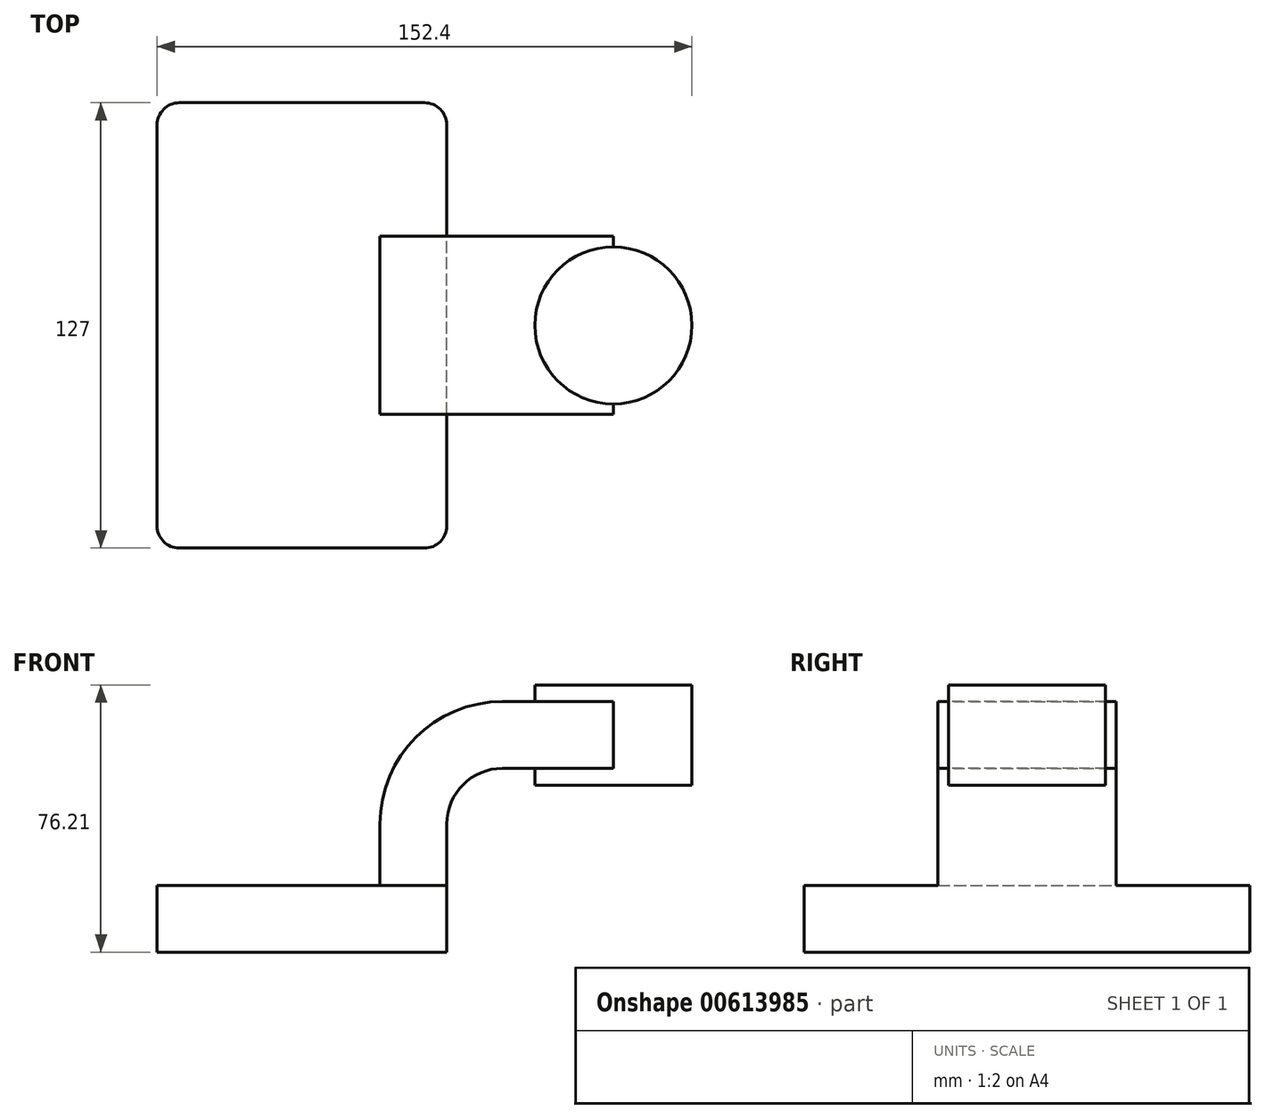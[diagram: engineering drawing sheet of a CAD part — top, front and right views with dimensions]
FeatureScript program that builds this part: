
annotation { "Feature Type Name" : "Feature", "Feature Type Description" : "" }
export const myFeature = defineFeature(function(context is Context, id is Id, definition is map)
    precondition{}
    {
        {
            var Q0;
            Q0=qCreatedBy(makeId("Front.planeOp"),FACE);
            var sketch = newSketch(context, id + "F0", { "sketchPlane" : qUnion([Q0])});
            skLineSegment(sketch, "E0.bottom", {"start": v(-41.28, -9.52) * mm, "end": v(41.28, -9.52) * mm});
            skLineSegment(sketch, "E0.top", {"start": v(-41.28, 9.53) * mm, "end": v(41.28, 9.53) * mm});
            skLineSegment(sketch, "E0.left", {"start": v(-41.27, -9.52) * mm, "end": v(-41.28, 9.53) * mm});
            skLineSegment(sketch, "E0.right", {"start": v(41.28, -9.52) * mm, "end": v(41.28, 9.53) * mm});
            skPoint(sketch, "E0.middle", {"position": v(0, 0) * mm});
            skLineSegment(sketch, "E1.bottom", {"start": v(60.32, 38.1) * mm, "end": v(111.12, 38.1) * mm});
            skLineSegment(sketch, "E1.top", {"start": v(60.32, 66.67) * mm, "end": v(111.12, 66.67) * mm});
            skLineSegment(sketch, "E1.left", {"start": v(60.32, 38.1) * mm, "end": v(60.32, 66.67) * mm});
            skLineSegment(sketch, "E1.right", {"start": v(111.12, 38.1) * mm, "end": v(111.12, 66.67) * mm});
            skPoint(sketch, "E1.middle", {"position": v(85.72, 52.39) * mm});
            skLineSegment(sketch, "E2", {"start": v(41.27, 9.53) * mm, "end": v(41.27, 27) * mm});
            skArc(sketch, "E3", {"start": v(41.27, 27) * mm, "mid": v(45.92, 38.23) * mm, "end": v(57.15, 42.88) * mm});
            skLineSegment(sketch, "E4", {"start": v(57.15, 42.88) * mm, "end": v(88.74, 42.88) * mm});
            skArc(sketch, "E5.0", {"start": v(22.22, 27) * mm, "mid": v(32.45, 51.7) * mm, "end": v(57.15, 61.93) * mm});
            skLineSegment(sketch, "E5.1", {"start": v(22.22, 9.53) * mm, "end": v(22.22, 27) * mm});
            skLineSegment(sketch, "E6.0", {"start": v(57.15, 61.93) * mm, "end": v(88.74, 61.93) * mm});
            skLineSegment(sketch, "E7", {"start": v(88.74, 42.88) * mm, "end": v(88.74, 61.93) * mm});
            skFitSpline(sketch, "E8", {"points": [v(-41.28, 9.53) * mm, v(57.15, 61.93) * mm], "startDerivative": vector(2.35, 60.88) * mm, "endDerivative": vector(125.28, -0.45) * mm});
            skLineSegment(sketch, "E9", {"start": v(88.74, 61.93) * mm, "end": v(88.74, 66.67) * mm});
            skLineSegment(sketch, "E10", {"start": v(88.74, 42.88) * mm, "end": v(88.74, 38.1) * mm});
            skSolve(sketch);
        }
        {
            var Q0;
            Q0=makeQuery(id+"F0.imprint","IMPRINT",FACE,{"disambiguationData":[TD([[makeQuery(id+"F0.imprint","IMPRINT",EDGE,{"derivedFrom":sQuery(id+"F0.wireOp",EDGE,"E0.bottom")}),1.0]])]});
            extrude(context, id + "F1", {"entities" : qUnion([Q0]), "endBound" : BoundingType.SYMMETRIC, "depth" : 127 * mm, "offsetDistance" : 25.4 * mm});
        }
        {
            var Q0;
            {var subQ0=sQuery(id+"F0.wireOp",EDGE,"E2");Q0=makeQuery(id+"F0.imprint","IMPRINT",FACE,{"disambiguationData":[TD([[makeQuery(id+"F0.imprint","IMPRINT",EDGE,{"derivedFrom":subQ0}),1.0]])]});}
            extrude(context, id + "F2", {"entities" : qUnion([Q0]), "operationType" : NewBodyOperationType.ADD, "endBound" : BoundingType.SYMMETRIC, "depth" : 50.8 * mm, "offsetDistance" : 25.4 * mm});
        }
        {
            var Q0;
            Q0=makeQuery(id+"F0.imprint","IMPRINT",FACE,{"disambiguationData":[TD([[makeQuery(id+"F0.imprint","IMPRINT",EDGE,{"derivedFrom":sQuery(id+"F0.wireOp",EDGE,"E5.0")}),1.0]])]});
            extrude(context, id + "F3", {"entities" : qUnion([Q0]), "operationType" : NewBodyOperationType.ADD, "endBound" : BoundingType.SYMMETRIC, "depth" : 15.88 * mm, "offsetDistance" : 25.4 * mm});
        }
        {
            var Q0;
            {var subQ5=sQuery(id+"F0.wireOp",EDGE,"E7");Q0=makeQuery(id+"F0.imprint","IMPRINT",FACE,{"disambiguationData":[TD([[makeQuery(id+"F0.imprint","IMPRINT",EDGE,{"derivedFrom":subQ5}),1.0]])]});}
            extrude(context, id + "F4", {"entities" : qUnion([Q0]), "operationType" : NewBodyOperationType.ADD, "endBound" : BoundingType.SYMMETRIC, "depth" : 50.8 * mm, "offsetDistance" : 25.4 * mm});
        }
        {
            var Q0;
            {var subQ0=sQuery(id+"F0.wireOp",EDGE,"E1.right");Q0=makeQuery(id+"F0.imprint","IMPRINT",FACE,{"disambiguationData":[TD([[makeQuery(id+"F0.imprint","IMPRINT",EDGE,{"derivedFrom":subQ0}),1.0]])]});}
            var Q1;
            Q1=sQuery(id+"F0.wireOp",EDGE,"E7");
            revolve(context, id + "F5", {"operationType" : NewBodyOperationType.ADD, "entities" : qUnion([Q0]), "axis" : qUnion([Q1]), "revolveType" : RevolveType.FULL});
        }
        {
            var Q0;
            Q0=makeQuery(id+"F1.opExtrude","CAP_EDGE",EDGE,{"disambiguationData":[OSD([sQuery(id+"F0.wireOp",EDGE,"E0.left")])],"isStart":false});
            var Q1;
            Q1=makeQuery(id+"F1.opExtrude","CAP_EDGE",EDGE,{"disambiguationData":[OSD([sQuery(id+"F0.wireOp",EDGE,"E0.right")])],"isStart":false});
            var Q2;
            Q2=makeQuery(id+"F1.opExtrude","CAP_EDGE",EDGE,{"disambiguationData":[OSD([sQuery(id+"F0.wireOp",EDGE,"E0.right")])],"isStart":true});
            var Q3;
            Q3=makeQuery(id+"F1.opExtrude","CAP_EDGE",EDGE,{"disambiguationData":[OSD([sQuery(id+"F0.wireOp",EDGE,"E0.left")])],"isStart":true});
            fillet(context, id + "F6", {"entities" : qUnion([Q0, Q1, Q2, Q3]), "radius" : 6.35 * mm, "tangentPropagation" : true, "allowEdgeOverflow" : false});
        }
    });
